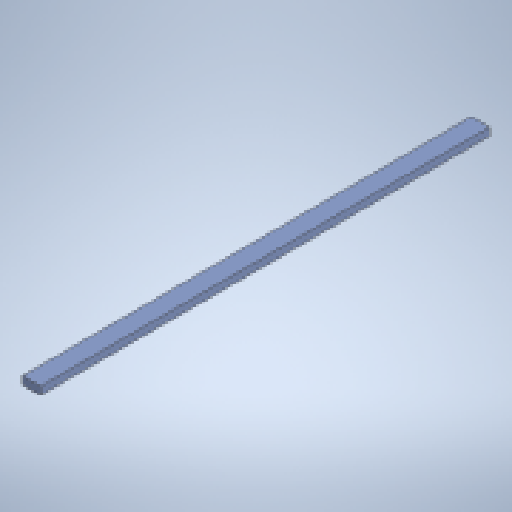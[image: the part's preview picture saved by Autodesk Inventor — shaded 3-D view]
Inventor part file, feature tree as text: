
AUTODESK INVENTOR PART (.ipt)
format: ipt  version: 2025.1 (Build 291241020, 241B)  size: 137,216 bytes
history: native  units: in
note: dims shown in document units (in); Inventor stores cm internally (conversion verified against a paired STEP export)
features: extrude x1, sketch x1, other x1
ambient origin geometry x8: Origin, YZ Plane, XZ Plane, XY Plane, X Axis, Y Axis, Z Axis, Center Point
bodies: Solid1 (feature_tree)
feature tree (3):
  extrude  "Extrusion1"  Depth=1.5in
  sketch  "Sketch1"  dims[d0=3.5in d1=1.5in d2=86.53in d3=0.0in]
  other  "Finish1"
